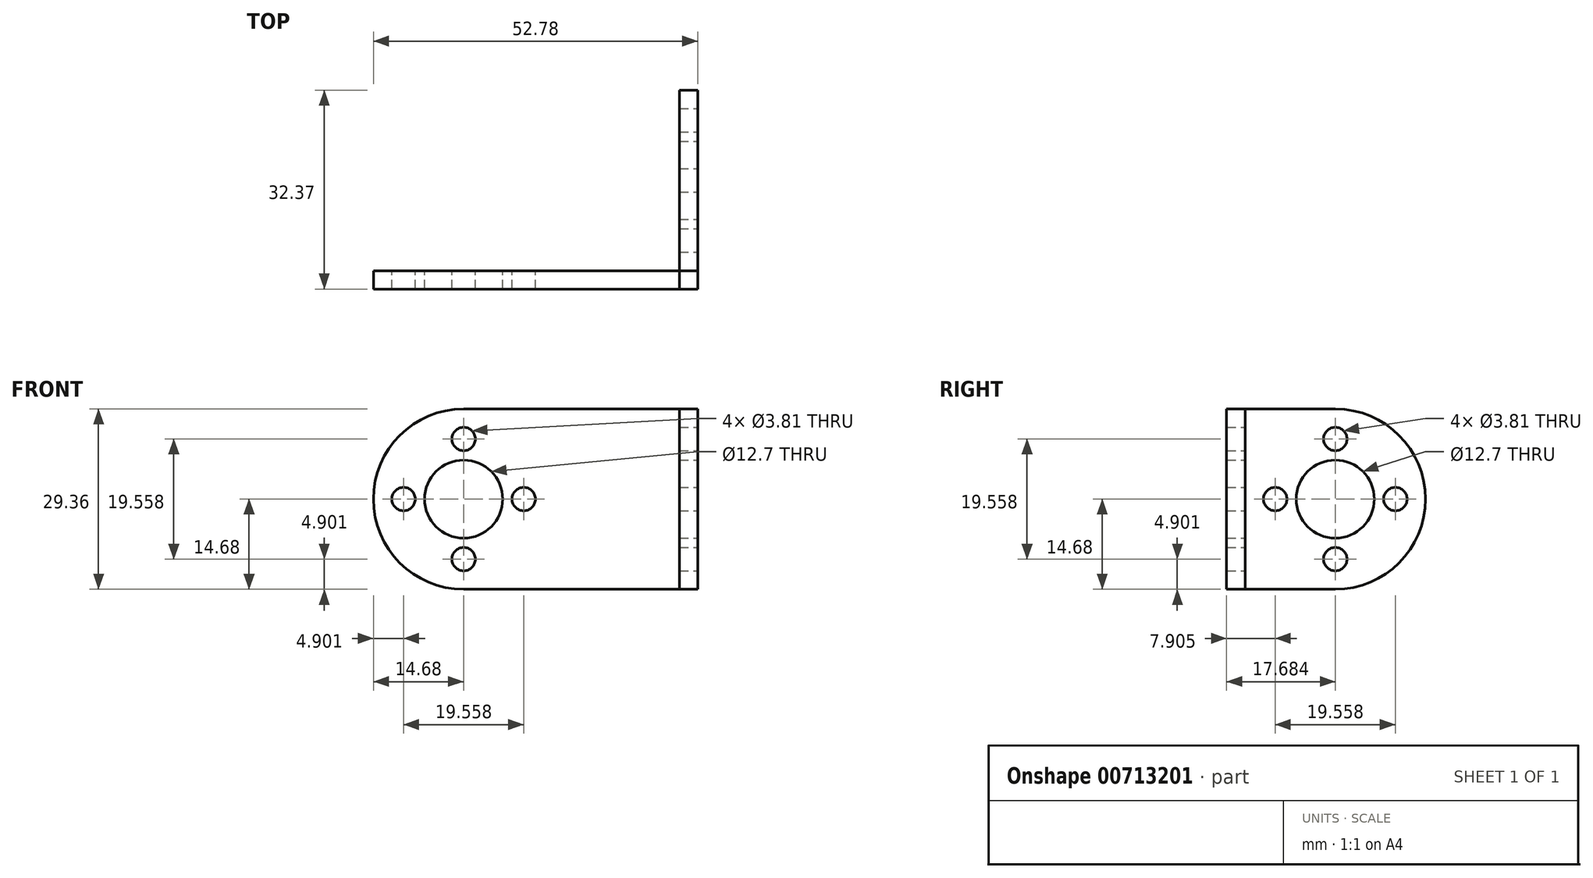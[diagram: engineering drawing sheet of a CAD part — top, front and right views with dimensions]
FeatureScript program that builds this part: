
annotation { "Feature Type Name" : "Feature", "Feature Type Description" : "" }
export const myFeature = defineFeature(function(context is Context, id is Id, definition is map)
    precondition{}
    {
        {
            var Q0;
            Q0=qCreatedBy(makeId("Front.planeOp"),FACE);
            var sketch = newSketch(context, id + "F0", { "sketchPlane" : qUnion([Q0])});
            skCircle(sketch, "E0", {"center": v(0, 0) * mm, "radius": 14.68 * mm});
            skCircle(sketch, "E1", {"center": v(0, 0) * mm, "radius": 9.78 * mm, "construction": true});
            skCircle(sketch, "E2", {"center": v(0, 9.78) * mm, "radius": 1.9 * mm});
            skCircle(sketch, "E3.1.0", {"center": v(-9.78, 0) * mm, "radius": 1.9 * mm});
            skCircle(sketch, "E3.2.0", {"center": v(0, -9.78) * mm, "radius": 1.9 * mm});
            skCircle(sketch, "E3.3.0", {"center": v(9.78, 0) * mm, "radius": 1.9 * mm});
            skCircle(sketch, "E4", {"center": v(0, 0) * mm, "radius": 6.35 * mm});
            skLineSegment(sketch, "E5", {"start": v(0, 14.68) * mm, "end": v(38.1, 14.68) * mm});
            skLineSegment(sketch, "E6", {"start": v(38.1, 14.68) * mm, "end": v(38.1, -14.68) * mm});
            skLineSegment(sketch, "E7", {"start": v(38.1, -14.68) * mm, "end": v(0, -14.68) * mm});
            skLineSegment(sketch, "E8", {"start": v(17.68, 14.68) * mm, "end": v(17.68, -14.68) * mm});
            skLineSegment(sketch, "E9", {"start": v(14.68, -14.68) * mm, "end": v(14.68, 14.68) * mm, "construction": true});
            skLineSegment(sketch, "E10", {"start": v(14.68, 0) * mm, "end": v(38.1, 0) * mm, "construction": true});
            skSolve(sketch);
        }
        {
            var Q0;
            {var subQ5=sQuery(id+"F0.wireOp",EDGE,"E6");Q0=makeQuery(id+"F0.imprint","IMPRINT",FACE,{"disambiguationData":[TD([[makeQuery(id+"F0.imprint","IMPRINT",EDGE,{"derivedFrom":subQ5}),-1.0]])]});}
            var Q1;
            {var subQ0=sQuery(id+"F0.wireOp",EDGE,"E5");var subQ1=sQuery(id+"F0.wireOp",EDGE,"E0");var subQ2=makeQuery(id+"F0.imprint","INTERSECT",VERTEX,{"derivedFrom":[subQ1,subQ0]});Q1=makeQuery(id+"F0.imprint","IMPRINT",FACE,{"disambiguationData":[TD([[makeQuery(id+"F0.imprint","IMPRINT",EDGE,{"disambiguationData":[TD([[subQ2,1.0]])],"derivedFrom":subQ1}),-1.0]])]});}
            var Q2;
            {var subQ0=sQuery(id+"F0.wireOp",EDGE,"E7");var subQ1=sQuery(id+"F0.wireOp",EDGE,"E0");var subQ2=makeQuery(id+"F0.imprint","INTERSECT",VERTEX,{"derivedFrom":[subQ1,subQ0]});Q2=makeQuery(id+"F0.imprint","IMPRINT",FACE,{"disambiguationData":[TD([[makeQuery(id+"F0.imprint","IMPRINT",EDGE,{"disambiguationData":[TD([[subQ2,-1.0]])],"derivedFrom":subQ1}),-1.0]])]});}
            var Q3;
            Q3=makeQuery(id+"F0.imprint","IMPRINT",FACE,{"disambiguationData":[TD([[makeQuery(id+"F0.imprint","IMPRINT",EDGE,{"derivedFrom":sQuery(id+"F0.wireOp",EDGE,"E2")}),-1.0]])]});
            extrude(context, id + "F1", {"entities" : qUnion([Q0, Q1, Q2, Q3]), "depth" : 3 * mm, "offsetDistance" : 25 * mm});
        }
        {
            var Q0;
            Q0=makeQuery(id+"F0.imprint","IMPRINT",FACE,{"disambiguationData":[TD([[makeQuery(id+"F0.imprint","IMPRINT",EDGE,{"derivedFrom":sQuery(id+"F0.wireOp",EDGE,"E2")}),-1.0]])]});
            var Q1;
            {var subQ5=sQuery(id+"F0.wireOp",EDGE,"E8");Q1=makeQuery(id+"F0.imprint","IMPRINT",FACE,{"disambiguationData":[TD([[makeQuery(id+"F0.imprint","IMPRINT",EDGE,{"derivedFrom":subQ5}),-1.0]])]});}
            extrude(context, id + "F2", {"entities" : qUnion([Q0, Q1]), "depth" : 3 * mm, "offsetDistance" : 25 * mm});
        }
        {
            var Q0;
            Q0=makeQuery(id+"F2.opExtrude","SWEPT_BODY",BODY,{"disambiguationData":[OSD([sQuery(id+"F0.wireOp",EDGE,"E0"),sQuery(id+"F0.wireOp",EDGE,"E2"),sQuery(id+"F0.wireOp",EDGE,"E3.1.0"),sQuery(id+"F0.wireOp",EDGE,"E3.2.0"),sQuery(id+"F0.wireOp",EDGE,"E3.3.0"),sQuery(id+"F0.wireOp",EDGE,"E4"),sQuery(id+"F0.wireOp",EDGE,"E5"),sQuery(id+"F0.wireOp",EDGE,"E7"),sQuery(id+"F0.wireOp",EDGE,"E8")])]});
            var Q1;
            Q1=sQuery(id+"F0.wireOp",EDGE,"E9");
            transform(context, id + "F3", {"entities" : qUnion([Q0]), "transformType" : TransformType.ROTATION, "transformAxis" : qUnion([Q1]), "angle" : 90 * degree, "oppositeDirection" : true, "makeCopy" : false});
        }
        {
            var Q0;
            Q0=makeQuery(id+"F2.opExtrude","SWEPT_BODY",BODY,{"disambiguationData":[OSD([sQuery(id+"F0.wireOp",EDGE,"E0"),sQuery(id+"F0.wireOp",EDGE,"E2"),sQuery(id+"F0.wireOp",EDGE,"E3.1.0"),sQuery(id+"F0.wireOp",EDGE,"E3.2.0"),sQuery(id+"F0.wireOp",EDGE,"E3.3.0"),sQuery(id+"F0.wireOp",EDGE,"E4"),sQuery(id+"F0.wireOp",EDGE,"E5"),sQuery(id+"F0.wireOp",EDGE,"E7"),sQuery(id+"F0.wireOp",EDGE,"E8")])]});
            var Q1;
            Q1=sQuery(id+"F0.wireOp",EDGE,"E10");
            transform(context, id + "F4", {"entities" : qUnion([Q0]), "transformType" : TransformType.TRANSLATION_ENTITY, "oppositeDirectionEntity" : false, "transformLine" : qUnion([Q1]), "makeCopy" : false});
        }
    });
